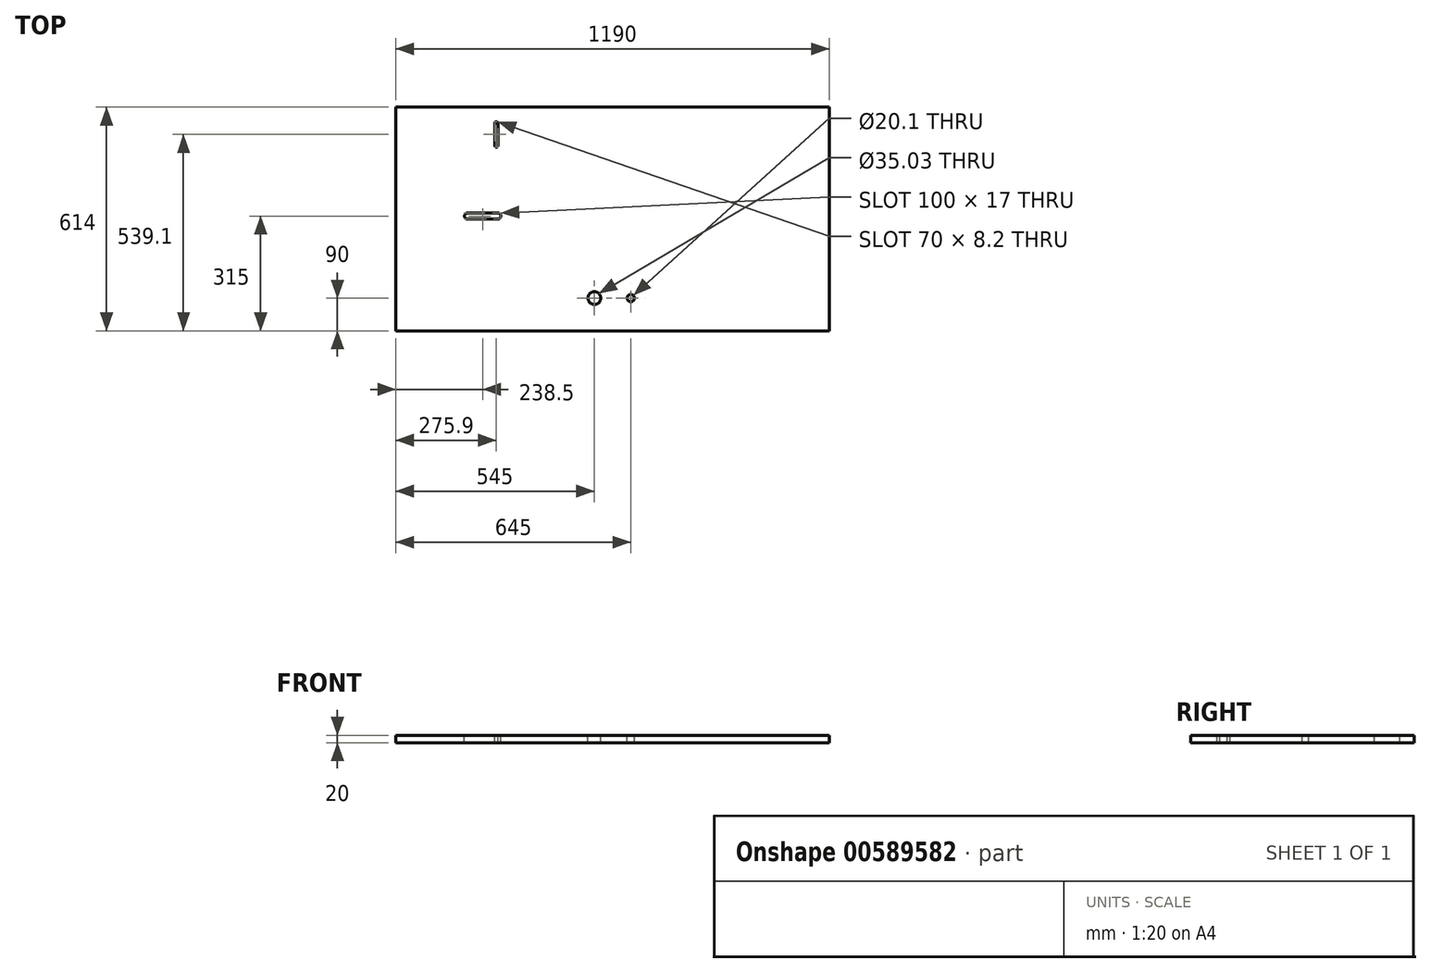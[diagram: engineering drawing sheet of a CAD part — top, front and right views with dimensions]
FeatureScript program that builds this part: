
annotation { "Feature Type Name" : "Feature", "Feature Type Description" : "" }
export const myFeature = defineFeature(function(context is Context, id is Id, definition is map)
    precondition{}
    {
        {
            var Q0;
            Q0=qCreatedBy(makeId("Top.planeOp"),FACE);
            var sketch = newSketch(context, id + "F0", { "sketchPlane" : qUnion([Q0])});
            skLineSegment(sketch, "E0.bottom", {"start": v(595, -315) * mm, "end": v(-595, -315) * mm});
            skLineSegment(sketch, "E0.top", {"start": v(595, 315) * mm, "end": v(-595, 315) * mm});
            skLineSegment(sketch, "E0.left", {"start": v(595, -315) * mm, "end": v(595, 315) * mm});
            skLineSegment(sketch, "E0.right", {"start": v(-595, -315) * mm, "end": v(-595, 315) * mm});
            skPoint(sketch, "E0.middle", {"position": v(0, 0) * mm});
            skSolve(sketch);
        }
        {
            var Q0;
            Q0 = qSketchRegion(id + "F0", true);
            extrude(context, id + "F1", {"entities" : qUnion([Q0]), "depth" : 20 * mm, "offsetDistance" : 25 * mm});
        }
        {
            var Q0;
            Q0=makeQuery(id+"F1.opExtrude","CAP_FACE",FACE,{"disambiguationData":[OSD([sQuery(id+"F0.wireOp",EDGE,"E0.bottom"),sQuery(id+"F0.wireOp",EDGE,"E0.top"),sQuery(id+"F0.wireOp",EDGE,"E0.left"),sQuery(id+"F0.wireOp",EDGE,"E0.right")])],"isStart":false});
            var sketch = newSketch(context, id + "F2", { "sketchPlane" : qUnion([Q0])});
            skLineSegment(sketch, "E1.bottom", {"start": v(315, -315) * mm, "end": v(-315, -315) * mm, "construction": true});
            skLineSegment(sketch, "E1.top", {"start": v(315, 315) * mm, "end": v(-315, 315) * mm, "construction": true});
            skLineSegment(sketch, "E1.left", {"start": v(315, -315) * mm, "end": v(315, 315) * mm, "construction": true});
            skLineSegment(sketch, "E1.right", {"start": v(-315, -315) * mm, "end": v(-315, 315) * mm, "construction": true});
            skPoint(sketch, "E1.middle", {"position": v(0, 0) * mm});
            skLineSegment(sketch, "E2", {"start": v(0, 0) * mm, "end": v(315, 0) * mm, "construction": true});
            skLineSegment(sketch, "E3", {"start": v(0, 0) * mm, "end": v(0, 315) * mm, "construction": true});
            skLineSegment(sketch, "E4.0", {"start": v(-285, -285) * mm, "end": v(-285, 285) * mm, "construction": true});
            skLineSegment(sketch, "E4.1", {"start": v(285, -285) * mm, "end": v(-285, -285) * mm, "construction": true});
            skLineSegment(sketch, "E4.2", {"start": v(285, -285) * mm, "end": v(285, 285) * mm, "construction": true});
            skLineSegment(sketch, "E4.3", {"start": v(285, 285) * mm, "end": v(-285, 285) * mm, "construction": true});
            skSolve(sketch);
        }
        {
            var Q0;
            Q0=makeQuery(id+"F2.imprint","IMPRINT",FACE,{"disambiguationData":[TD([[makeQuery(id+"F2.imprint","IMPRINT",EDGE,{"derivedFrom":makeQuery(id+"F1.opExtrude","CAP_EDGE",EDGE,{"disambiguationData":[OSD([sQuery(id+"F0.wireOp",EDGE,"E0.bottom")])],"isStart":false})}),-1.0]])]});
            var sketch = newSketch(context, id + "F3", { "sketchPlane" : qUnion([Q0])});
            skArc(sketch, "E5", {"start": v(-315, -8.5) * mm, "mid": v(-306.5, 0) * mm, "end": v(-315, 8.5) * mm});
            skArc(sketch, "E6", {"start": v(-398, 8.5) * mm, "mid": v(-406.5, 0) * mm, "end": v(-398, -8.5) * mm});
            skLineSegment(sketch, "E7", {"start": v(-398, 8.5) * mm, "end": v(-315, 8.5) * mm});
            skLineSegment(sketch, "E8", {"start": v(-315, 8.5) * mm, "end": v(-315, -8.5) * mm, "construction": true});
            skLineSegment(sketch, "E9", {"start": v(-315, -8.5) * mm, "end": v(-398, -8.5) * mm});
            skLineSegment(sketch, "E10", {"start": v(-398, -8.5) * mm, "end": v(-398, 8.5) * mm, "construction": true});
            skArc(sketch, "E11", {"start": v(-323.2, 193.2) * mm, "mid": v(-319.1, 189.1) * mm, "end": v(-315, 193.2) * mm});
            skArc(sketch, "E12", {"start": v(-315, 255) * mm, "mid": v(-319.1, 259.1) * mm, "end": v(-323.2, 255) * mm});
            skLineSegment(sketch, "E13", {"start": v(-315, 255) * mm, "end": v(-315, 193.2) * mm});
            skLineSegment(sketch, "E14", {"start": v(-315, 193.2) * mm, "end": v(-323.2, 193.2) * mm, "construction": true});
            skLineSegment(sketch, "E15", {"start": v(-323.2, 193.2) * mm, "end": v(-323.2, 255) * mm});
            skLineSegment(sketch, "E16", {"start": v(-323.2, 255) * mm, "end": v(-315, 255) * mm, "construction": true});
            skSolve(sketch);
        }
        {
            var Q0;
            Q0=makeQuery(id+"F3.imprint","IMPRINT",FACE,{"disambiguationData":[TD([[makeQuery(id+"F3.imprint","IMPRINT",EDGE,{"derivedFrom":sQuery(id+"F3.wireOp",EDGE,"E11")}),1.0]])]});
            extrude(context, id + "F4", {"entities" : qUnion([Q0]), "operationType" : NewBodyOperationType.REMOVE, "endBound" : BoundingType.THROUGH_ALL, "oppositeDirection" : true, "depth" : 25 * mm, "offsetDistance" : 25 * mm});
        }
        {
            var Q0;
            Q0=makeQuery(id+"F3.imprint","IMPRINT",FACE,{"disambiguationData":[TD([[makeQuery(id+"F3.imprint","IMPRINT",EDGE,{"derivedFrom":sQuery(id+"F3.wireOp",EDGE,"E5")}),1.0]])]});
            extrude(context, id + "F5", {"entities" : qUnion([Q0]), "operationType" : NewBodyOperationType.REMOVE, "endBound" : BoundingType.THROUGH_ALL, "oppositeDirection" : true, "depth" : 25 * mm, "offsetDistance" : 25 * mm});
        }
        {
            var Q0;
            Q0=qCreatedBy(makeId("Front.planeOp"),FACE);
            var sketch = newSketch(context, id + "F6", { "sketchPlane" : qUnion([Q0])});
            skLineSegment(sketch, "E17", {"start": v(0, 0) * mm, "end": v(0, 74.28) * mm, "construction": true});
            skSolve(sketch);
        }
        {
            var Q0;
            Q0=makeQuery(id+"F2.imprint","IMPRINT",FACE,{"disambiguationData":[TD([[makeQuery(id+"F2.imprint","IMPRINT",EDGE,{"derivedFrom":makeQuery(id+"F1.opExtrude","CAP_EDGE",EDGE,{"disambiguationData":[OSD([sQuery(id+"F0.wireOp",EDGE,"E0.bottom")])],"isStart":false})}),-1.0]])]});
            var sketch = newSketch(context, id + "F7", { "sketchPlane" : qUnion([Q0])});
            skCircle(sketch, "E18", {"center": v(-50, -225) * mm, "radius": 17.52 * mm});
            skCircle(sketch, "E19", {"center": v(50, -225) * mm, "radius": 10.05 * mm});
            skSolve(sketch);
        }
        {
            var Q0;
            Q0 = qSketchRegion(id + "F7", true);
            extrude(context, id + "F8", {"entities" : qUnion([Q0]), "operationType" : NewBodyOperationType.REMOVE, "endBound" : BoundingType.THROUGH_ALL, "oppositeDirection" : true, "depth" : 25 * mm, "offsetDistance" : 25 * mm});
        }
        {
            var Q0;
            Q0=makeQuery(id+"F2.imprint","IMPRINT",FACE,{"disambiguationData":[TD([[makeQuery(id+"F2.imprint","IMPRINT",EDGE,{"derivedFrom":makeQuery(id+"F1.opExtrude","CAP_EDGE",EDGE,{"disambiguationData":[OSD([sQuery(id+"F0.wireOp",EDGE,"E0.bottom")])],"isStart":false})}),-1.0]])]});
            var sketch = newSketch(context, id + "F9", { "sketchPlane" : qUnion([Q0])});
            skLineSegment(sketch, "E20.bottom", {"start": v(595, 299) * mm, "end": v(-595, 299) * mm});
            skLineSegment(sketch, "E20.top", {"start": v(595, 557.44) * mm, "end": v(-595, 557.44) * mm});
            skLineSegment(sketch, "E20.left", {"start": v(595, 299) * mm, "end": v(595, 557.44) * mm});
            skLineSegment(sketch, "E20.right", {"start": v(-595, 299) * mm, "end": v(-595, 557.44) * mm});
            skPoint(sketch, "E20.middle", {"position": v(0, 428.22) * mm});
            skSolve(sketch);
        }
        {
            var Q0;
            Q0=makeQuery(id+"F2.imprint","IMPRINT",FACE,{"disambiguationData":[TD([[makeQuery(id+"F2.imprint","IMPRINT",EDGE,{"derivedFrom":makeQuery(id+"F1.opExtrude","CAP_EDGE",EDGE,{"disambiguationData":[OSD([sQuery(id+"F0.wireOp",EDGE,"E0.bottom")])],"isStart":false})}),-1.0]])]});
            var sketch = newSketch(context, id + "F10", { "sketchPlane" : qUnion([Q0])});
            skLineSegment(sketch, "E21.0", {"start": v(-308, -308) * mm, "end": v(-308, 308) * mm, "construction": true});
            skLineSegment(sketch, "E21.1", {"start": v(308, -308) * mm, "end": v(-308, -308) * mm, "construction": true});
            skLineSegment(sketch, "E21.2", {"start": v(308, -308) * mm, "end": v(308, 308) * mm, "construction": true});
            skLineSegment(sketch, "E21.3", {"start": v(308, 308) * mm, "end": v(-308, 308) * mm, "construction": true});
            skSolve(sketch);
        }
        {
            var Q0;
            Q0=makeQuery(id+"F2.imprint","IMPRINT",FACE,{"disambiguationData":[TD([[makeQuery(id+"F2.imprint","IMPRINT",EDGE,{"derivedFrom":makeQuery(id+"F1.opExtrude","CAP_EDGE",EDGE,{"disambiguationData":[OSD([sQuery(id+"F0.wireOp",EDGE,"E0.bottom")])],"isStart":false})}),-1.0]])]});
            var sketch = newSketch(context, id + "F11", { "sketchPlane" : qUnion([Q0])});
            skCircle(sketch, "E22", {"center": v(-308, 308) * mm, "radius": 2.5 * mm});
            skCircle(sketch, "E23", {"center": v(-184.8, 308) * mm, "radius": 2.5 * mm});
            skCircle(sketch, "E24", {"center": v(-61.6, 308) * mm, "radius": 2.5 * mm});
            skLineSegment(sketch, "E25", {"start": v(-308, 308) * mm, "end": v(-184.8, 308) * mm, "construction": true});
            skLineSegment(sketch, "E26", {"start": v(-184.8, 308) * mm, "end": v(-61.6, 308) * mm, "construction": true});
            skPoint(sketch, "E27", {"position": v(0, 308) * mm});
            skLineSegment(sketch, "E28.trimOffspring", {"start": v(0, 308) * mm, "end": v(-61.6, 308) * mm, "construction": true});
            skCircle(sketch, "E29.MirrorC", {"center": v(61.6, 308) * mm, "radius": 2.5 * mm});
            skCircle(sketch, "E30.MirrorC", {"center": v(184.8, 308) * mm, "radius": 2.5 * mm});
            skCircle(sketch, "E31.MirrorC", {"center": v(308, 308) * mm, "radius": 2.5 * mm});
            skSolve(sketch);
        }
        {
            var Q0;
            Q0 = qSketchRegion(id + "F11", true);
            extrude(context, id + "F12", {"entities" : qUnion([Q0]), "operationType" : NewBodyOperationType.REMOVE, "endBound" : BoundingType.THROUGH_ALL, "oppositeDirection" : true, "depth" : 25 * mm, "offsetDistance" : 25 * mm});
        }
        {
            var Q0;
            Q0 = qSketchRegion(id + "F9", true);
            extrude(context, id + "F13", {"entities" : qUnion([Q0]), "operationType" : NewBodyOperationType.REMOVE, "endBound" : BoundingType.THROUGH_ALL, "oppositeDirection" : true, "depth" : 25 * mm, "offsetDistance" : 25 * mm});
        }
    });
